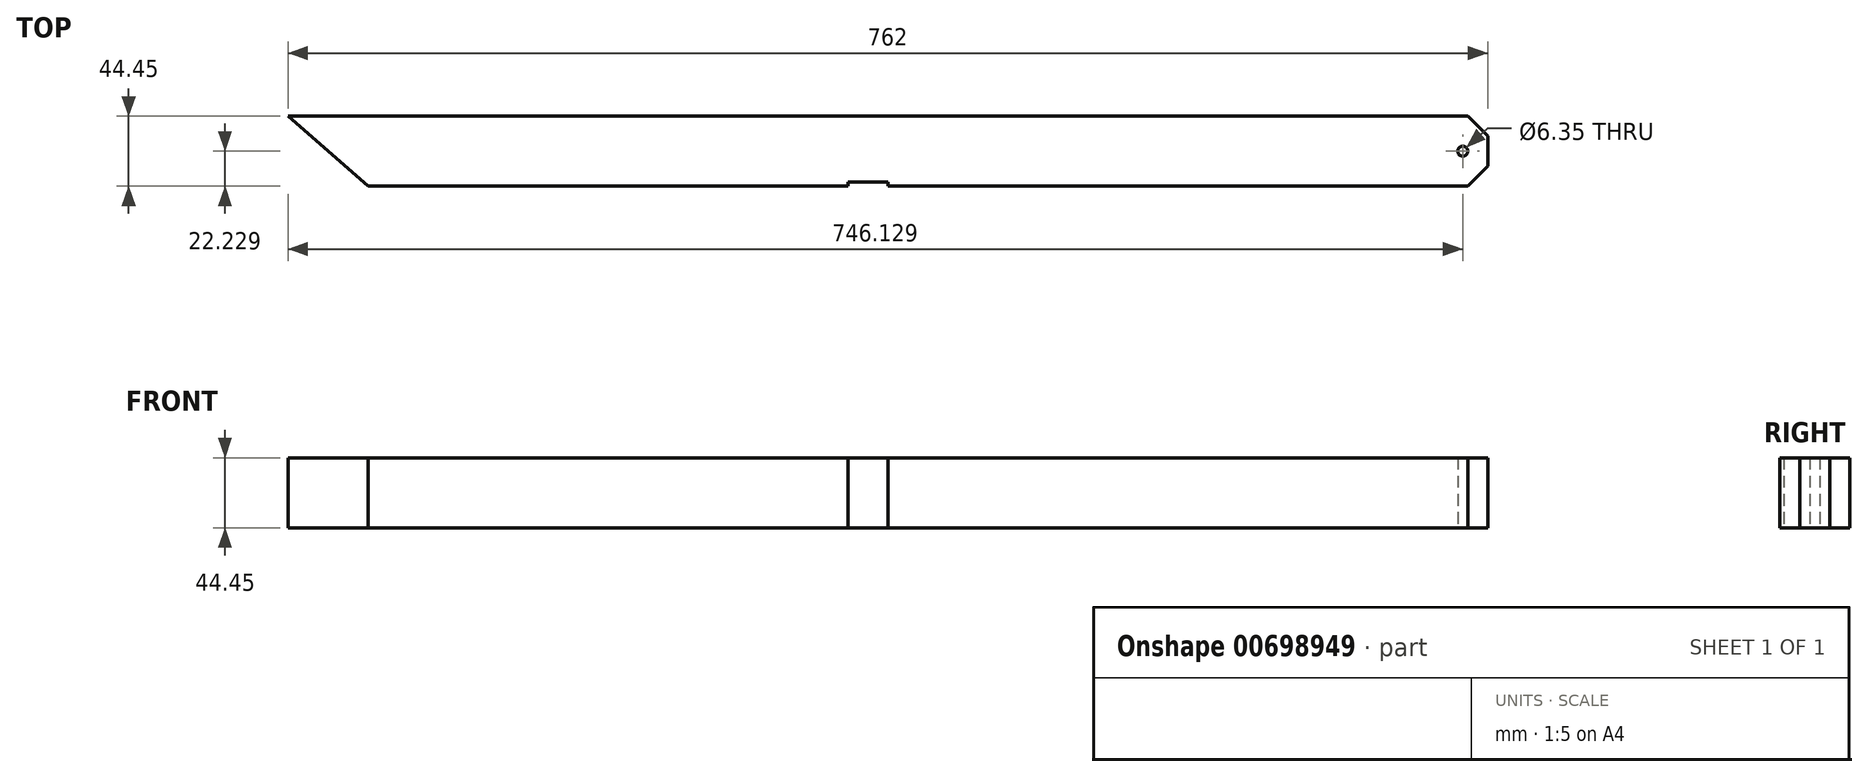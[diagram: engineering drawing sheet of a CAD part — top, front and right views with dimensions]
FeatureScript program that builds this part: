
annotation { "Feature Type Name" : "Feature", "Feature Type Description" : "" }
export const myFeature = defineFeature(function(context is Context, id is Id, definition is map)
    precondition{}
    {
        {
            var Q0;
            Q0=qCreatedBy(makeId("Top.planeOp"),FACE);
            var sketch = newSketch(context, id + "F0", { "sketchPlane" : qUnion([Q0])});
            skCircle(sketch, "E0", {"center": v(451.4, 48.6) * mm, "radius": 3.18 * mm});
            skLineSegment(sketch, "E1", {"start": v(60.88, 26.38) * mm, "end": v(60.88, 28.92) * mm});
            skLineSegment(sketch, "E2", {"start": v(60.88, 28.92) * mm, "end": v(86.28, 28.92) * mm});
            skLineSegment(sketch, "E3", {"start": v(86.28, 28.92) * mm, "end": v(86.28, 26.38) * mm});
            skLineSegment(sketch, "E4", {"start": v(-294.72, 70.83) * mm, "end": v(-243.92, 26.38) * mm});
            skLineSegment(sketch, "E5", {"start": v(454.58, 70.83) * mm, "end": v(467.28, 58.13) * mm});
            skLineSegment(sketch, "E6", {"start": v(467.28, 58.13) * mm, "end": v(467.28, 39.08) * mm});
            skLineSegment(sketch, "E7", {"start": v(467.28, 39.08) * mm, "end": v(454.58, 26.38) * mm});
            skLineSegment(sketch, "E8", {"start": v(454.58, 26.38) * mm, "end": v(-243.92, 26.38) * mm});
            skLineSegment(sketch, "E9", {"start": v(454.58, 70.83) * mm, "end": v(-294.72, 70.83) * mm});
            skSolve(sketch);
        }
        {
            var Q0;
            Q0=makeQuery(id+"F0.imprint","IMPRINT",FACE,{"disambiguationData":[TD([[makeQuery(id+"F0.imprint","IMPRINT",EDGE,{"derivedFrom":sQuery(id+"F0.wireOp",EDGE,"E0")}),-1.0]])]});
            extrude(context, id + "F1", {"entities" : qUnion([Q0]), "depth" : 44.45 * mm, "offsetDistance" : 25.4 * mm});
        }
    });
